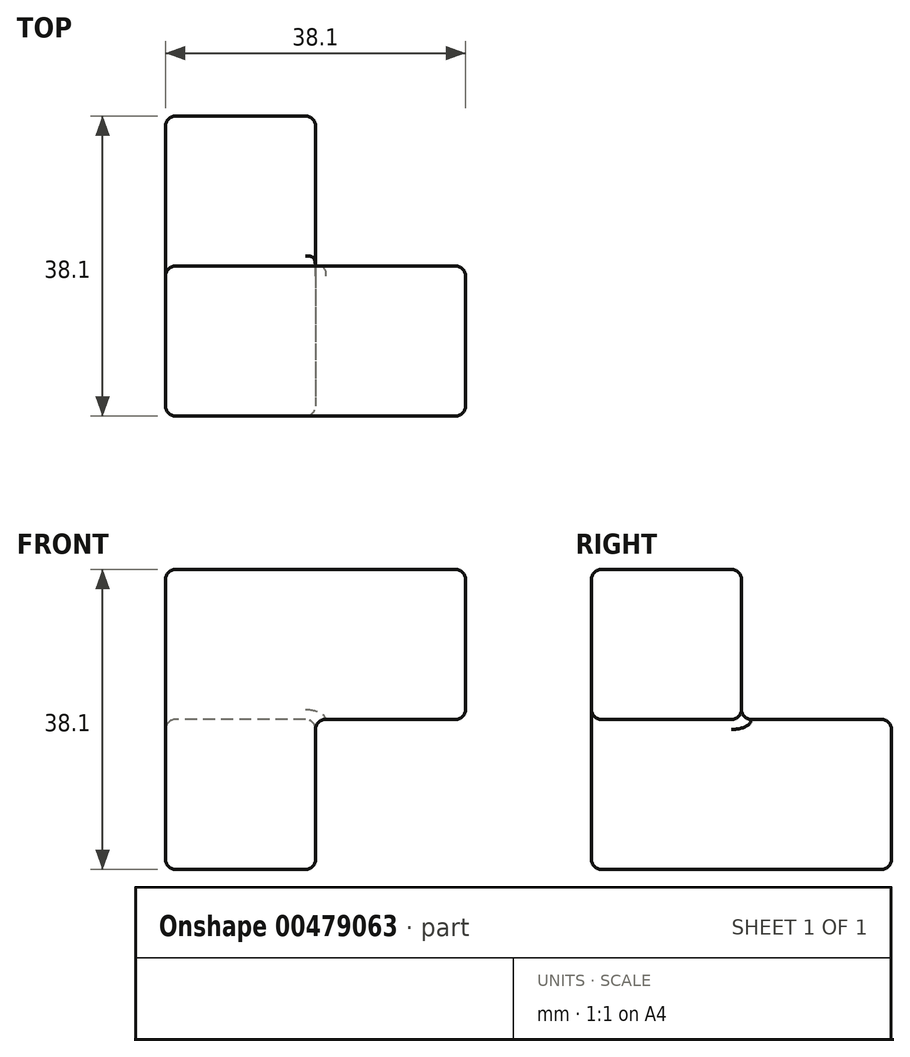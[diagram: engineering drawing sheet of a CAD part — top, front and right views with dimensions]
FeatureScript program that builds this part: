
annotation { "Feature Type Name" : "Feature", "Feature Type Description" : "" }
export const myFeature = defineFeature(function(context is Context, id is Id, definition is map)
    precondition{}
    {
        {
            var Q0;
            Q0=qCreatedBy(makeId("Top.planeOp"),FACE);
            var sketch = newSketch(context, id + "F0", { "sketchPlane" : qUnion([Q0])});
            skLineSegment(sketch, "E0.bottom", {"start": v(0, 19.05) * mm, "end": v(-19.05, 19.05) * mm});
            skLineSegment(sketch, "E0.top", {"start": v(0, -19.05) * mm, "end": v(-19.05, -19.05) * mm});
            skLineSegment(sketch, "E0.left", {"start": v(0, 19.05) * mm, "end": v(0, -19.05) * mm});
            skLineSegment(sketch, "E0.right", {"start": v(-19.05, 19.05) * mm, "end": v(-19.05, -19.05) * mm});
            skSolve(sketch);
        }
        {
            var Q0;
            Q0 = qSketchRegion(id + "F0", true);
            extrude(context, id + "F1", {"entities" : qUnion([Q0]), "oppositeDirection" : true, "depth" : 19.05 * mm});
        }
        {
            var Q0;
            Q0=makeQuery(id+"F1.opExtrude","CAP_FACE",FACE,{"disambiguationData":[OSD([sQuery(id+"F0.wireOp",EDGE,"E0.bottom"),sQuery(id+"F0.wireOp",EDGE,"E0.top"),sQuery(id+"F0.wireOp",EDGE,"E0.left"),sQuery(id+"F0.wireOp",EDGE,"E0.right")])],"isStart":true});
            var sketch = newSketch(context, id + "F2", { "sketchPlane" : qUnion([Q0])});
            skLineSegment(sketch, "E1.bottom", {"start": v(-19.05, -19.05) * mm, "end": v(19.05, -19.05) * mm});
            skLineSegment(sketch, "E1.top", {"start": v(-19.05, 0) * mm, "end": v(19.05, 0) * mm});
            skLineSegment(sketch, "E1.left", {"start": v(-19.05, -19.05) * mm, "end": v(-19.05, 0) * mm});
            skLineSegment(sketch, "E1.right", {"start": v(19.05, -19.05) * mm, "end": v(19.05, 0) * mm});
            skSolve(sketch);
        }
        {
            var Q0;
            Q0 = qSketchRegion(id + "F2", true);
            extrude(context, id + "F3", {"entities" : qUnion([Q0]), "operationType" : NewBodyOperationType.ADD, "depth" : 19.05 * mm});
        }
        {
            var Q0;
            Q0=makeQuery(id+"F3.opExtrude","SWEPT_FACE",FACE,{"disambiguationData":[OSD([sQuery(id+"F2.wireOp",EDGE,"E1.right")])]});
            var Q1;
            Q1=makeQuery(id+"F3.opExtrude","CAP_FACE",FACE,{"disambiguationData":[OSD([sQuery(id+"F2.wireOp",EDGE,"E1.bottom"),sQuery(id+"F2.wireOp",EDGE,"E1.top"),sQuery(id+"F2.wireOp",EDGE,"E1.left"),sQuery(id+"F2.wireOp",EDGE,"E1.right")])],"isStart":true});
            var Q2;
            Q2=makeQuery(id+"F1.opExtrude","SWEPT_FACE",FACE,{"disambiguationData":[OSD([sQuery(id+"F0.wireOp",EDGE,"E0.left")])]});
            var Q3;
            Q3=makeQuery(id+"F1.opExtrude","CAP_FACE",FACE,{"disambiguationData":[OSD([sQuery(id+"F0.wireOp",EDGE,"E0.bottom"),sQuery(id+"F0.wireOp",EDGE,"E0.top"),sQuery(id+"F0.wireOp",EDGE,"E0.left"),sQuery(id+"F0.wireOp",EDGE,"E0.right")])],"isStart":false});
            var Q4;
            Q4=makeQuery(id+"F1.opExtrude","SWEPT_FACE",FACE,{"disambiguationData":[OSD([sQuery(id+"F0.wireOp",EDGE,"E0.bottom")])]});
            var Q5;
            Q5=makeQuery(id+"F1.opExtrude","CAP_FACE",FACE,{"disambiguationData":[OSD([sQuery(id+"F0.wireOp",EDGE,"E0.bottom"),sQuery(id+"F0.wireOp",EDGE,"E0.top"),sQuery(id+"F0.wireOp",EDGE,"E0.left"),sQuery(id+"F0.wireOp",EDGE,"E0.right")])],"isStart":true});
            var Q6;
            Q6=makeQuery(id+"F3.opExtrude","SWEPT_FACE",FACE,{"disambiguationData":[OSD([sQuery(id+"F2.wireOp",EDGE,"E1.top")])]});
            var Q7;
            Q7=makeQuery(id+"F3.opExtrude","CAP_FACE",FACE,{"disambiguationData":[OSD([sQuery(id+"F2.wireOp",EDGE,"E1.bottom"),sQuery(id+"F2.wireOp",EDGE,"E1.top"),sQuery(id+"F2.wireOp",EDGE,"E1.left"),sQuery(id+"F2.wireOp",EDGE,"E1.right")])],"isStart":false});
            var Q8;
            Q8=makeQuery(id+"F3.boolean.opBoolean","MERGE",FACE,{"derivedFrom":[makeQuery(id+"F1.opExtrude","SWEPT_FACE",FACE,{"disambiguationData":[OSD([sQuery(id+"F0.wireOp",EDGE,"E0.top")])]}),makeQuery(id+"F3.opExtrude","SWEPT_FACE",FACE,{"disambiguationData":[OSD([sQuery(id+"F2.wireOp",EDGE,"E1.bottom")])]})]});
            var Q9;
            Q9=makeQuery(id+"F3.boolean.opBoolean","MERGE",FACE,{"derivedFrom":[makeQuery(id+"F1.opExtrude","SWEPT_FACE",FACE,{"disambiguationData":[OSD([sQuery(id+"F0.wireOp",EDGE,"E0.right")])]}),makeQuery(id+"F3.opExtrude","SWEPT_FACE",FACE,{"disambiguationData":[OSD([sQuery(id+"F2.wireOp",EDGE,"E1.left")])]})]});
            fillet(context, id + "F4", {"entities" : qUnion([Q0, Q1, Q2, Q3, Q4, Q5, Q6, Q7, Q8, Q9]), "radius" : 1.27 * mm, "tangentPropagation" : true, "allowEdgeOverflow" : false});
        }
    });
